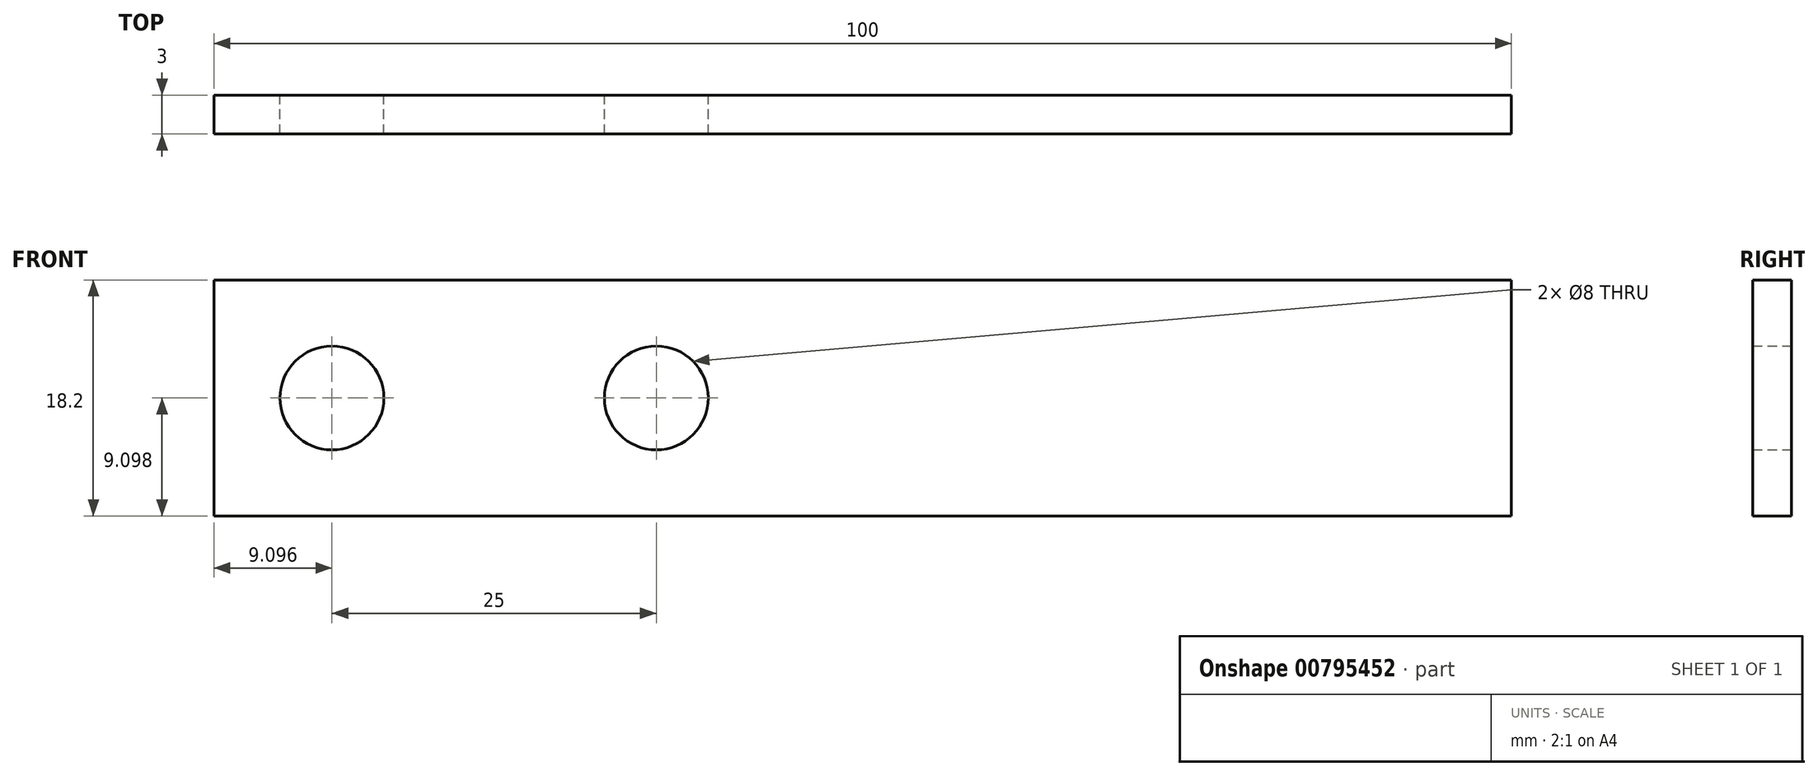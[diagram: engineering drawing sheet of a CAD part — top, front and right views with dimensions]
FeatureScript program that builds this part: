
annotation { "Feature Type Name" : "Feature", "Feature Type Description" : "" }
export const myFeature = defineFeature(function(context is Context, id is Id, definition is map)
    precondition{}
    {
        {
            var Q0;
            Q0=qCreatedBy(makeId("Front.planeOp"),FACE);
            var sketch = newSketch(context, id + "F0", { "sketchPlane" : qUnion([Q0])});
            skLineSegment(sketch, "E0.bottom", {"start": v(-52.82, 5.5) * mm, "end": v(47.18, 5.5) * mm});
            skLineSegment(sketch, "E0.top", {"start": v(-52.82, -12.7) * mm, "end": v(47.18, -12.7) * mm});
            skLineSegment(sketch, "E0.left", {"start": v(-52.82, 5.5) * mm, "end": v(-52.82, -12.7) * mm});
            skLineSegment(sketch, "E0.right", {"start": v(47.18, 5.5) * mm, "end": v(47.18, -12.7) * mm});
            skPoint(sketch, "E1", {"position": v(-43.72, -3.6) * mm});
            skPoint(sketch, "E1.positionSnap0", {"position": v(-52.82, -3.6) * mm});
            skPoint(sketch, "E2", {"position": v(-18.72, -3.6) * mm});
            skCircle(sketch, "E3", {"center": v(-43.72, -3.6) * mm, "radius": 4 * mm});
            skCircle(sketch, "E4", {"center": v(-18.72, -3.6) * mm, "radius": 4 * mm});
            skSolve(sketch);
        }
        {
            var Q0;
            Q0=qSketchRegion(id+"F0",true);
            var Q1;
            Q1=makeQuery(id+"F0.imprint","IMPRINT",FACE,{"disambiguationData":[TD([[makeQuery(id+"F0.imprint","IMPRINT",EDGE,{"derivedFrom":sQuery(id+"F0.wireOp",EDGE,"E0.bottom")}),-1.0]])]});
            extrude(context, id + "F1", {"entities" : qUnion([Q0, Q1]), "depth" : 3 * mm, "offsetDistance" : 25 * mm});
        }
    });
